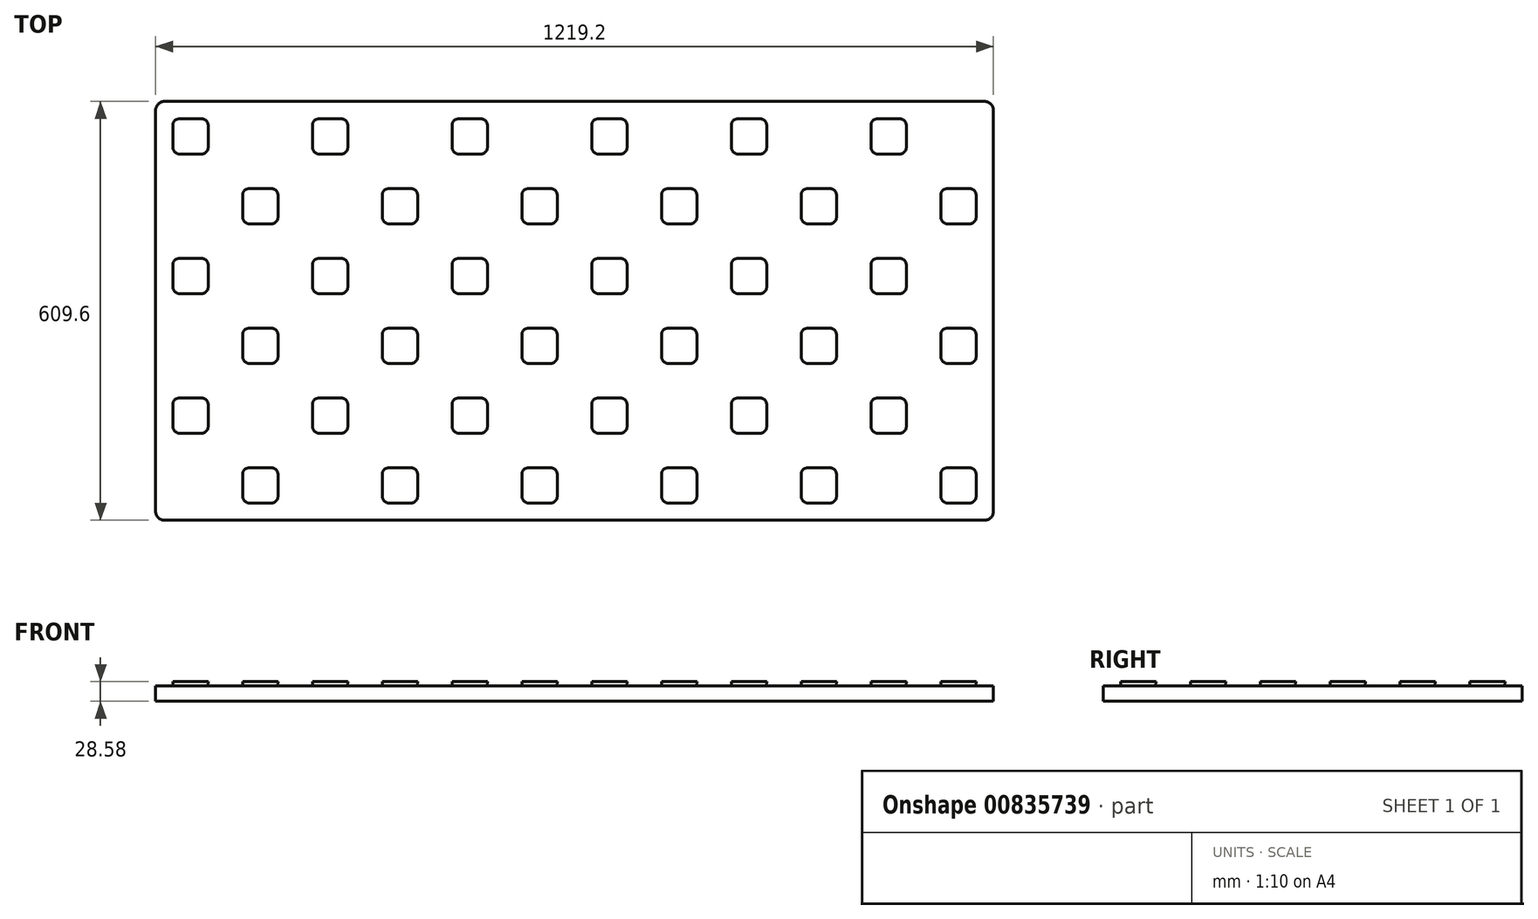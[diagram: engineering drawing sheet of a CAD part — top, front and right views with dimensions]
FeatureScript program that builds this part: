
annotation { "Feature Type Name" : "Feature", "Feature Type Description" : "" }
export const myFeature = defineFeature(function(context is Context, id is Id, definition is map)
    precondition{}
    {
        {
            var Q0;
            Q0=qCreatedBy(makeId("Top.planeOp"),FACE);
            var sketch = newSketch(context, id + "F0", { "sketchPlane" : qUnion([Q0])});
            skLineSegment(sketch, "E0.bottom", {"start": v(12.7, 0) * mm, "end": v(1206.5, 0) * mm});
            skLineSegment(sketch, "E0.top", {"start": v(12.7, 609.6) * mm, "end": v(1206.5, 609.6) * mm});
            skLineSegment(sketch, "E0.left", {"start": v(0, 12.7) * mm, "end": v(0, 596.9) * mm});
            skLineSegment(sketch, "E0.right", {"start": v(1219.2, 12.7) * mm, "end": v(1219.2, 596.9) * mm});
            skPoint(sketch, "E1.visualSharp", {"position": v(0, 609.6) * mm});
            skArc(sketch, "E1.filletArc", {"start": v(12.7, 609.6) * mm, "mid": v(3.72, 605.88) * mm, "end": v(0, 596.9) * mm});
            skPoint(sketch, "E2.visualSharp", {"position": v(1219.2, 609.6) * mm});
            skArc(sketch, "E2.filletArc", {"start": v(1219.2, 596.9) * mm, "mid": v(1215.48, 605.88) * mm, "end": v(1206.5, 609.6) * mm});
            skPoint(sketch, "E3.visualSharp", {"position": v(1219.2, 0) * mm});
            skArc(sketch, "E3.filletArc", {"start": v(1206.5, 0) * mm, "mid": v(1215.48, 3.72) * mm, "end": v(1219.2, 12.7) * mm});
            skPoint(sketch, "E4.visualSharp", {"position": v(0, 0) * mm});
            skArc(sketch, "E4.filletArc", {"start": v(0, 12.7) * mm, "mid": v(3.72, 3.72) * mm, "end": v(12.7, 0) * mm});
            skSolve(sketch);
        }
        {
            var Q0;
            Q0 = qSketchRegion(id + "F0", true);
            extrude(context, id + "F1", {"entities" : qUnion([Q0]), "depth" : 22.22 * mm, "offsetDistance" : 25.4 * mm});
        }
        {
            var Q0;
            Q0=makeQuery(id+"F1.opExtrude","CAP_FACE",FACE,{"disambiguationData":[OSD([sQuery(id+"F0.wireOp",EDGE,"E0.bottom"),sQuery(id+"F0.wireOp",EDGE,"E0.top"),sQuery(id+"F0.wireOp",EDGE,"E0.left"),sQuery(id+"F0.wireOp",EDGE,"E0.right"),sQuery(id+"F0.wireOp",EDGE,"E1.filletArc"),sQuery(id+"F0.wireOp",EDGE,"E2.filletArc"),sQuery(id+"F0.wireOp",EDGE,"E3.filletArc"),sQuery(id+"F0.wireOp",EDGE,"E4.filletArc")])],"isStart":false});
            var sketch = newSketch(context, id + "F2", { "sketchPlane" : qUnion([Q0])});
            skLineSegment(sketch, "E5.bottom", {"start": v(66.67, 584.2) * mm, "end": v(34.93, 584.2) * mm});
            skLineSegment(sketch, "E5.top", {"start": v(66.68, 533.4) * mm, "end": v(34.93, 533.4) * mm});
            skLineSegment(sketch, "E5.left", {"start": v(76.2, 574.68) * mm, "end": v(76.2, 542.93) * mm});
            skLineSegment(sketch, "E5.right", {"start": v(25.4, 574.68) * mm, "end": v(25.4, 542.93) * mm});
            skPoint(sketch, "E5.middle", {"position": v(50.8, 558.8) * mm});
            skPoint(sketch, "E6.visualSharp", {"position": v(25.4, 584.2) * mm});
            skArc(sketch, "E6.filletArc", {"start": v(34.93, 584.2) * mm, "mid": v(28.19, 581.41) * mm, "end": v(25.4, 574.68) * mm});
            skPoint(sketch, "E7.visualSharp", {"position": v(76.2, 533.4) * mm});
            skArc(sketch, "E7.filletArc", {"start": v(66.68, 533.4) * mm, "mid": v(73.41, 536.19) * mm, "end": v(76.2, 542.93) * mm});
            skPoint(sketch, "E8.visualSharp", {"position": v(25.4, 533.4) * mm});
            skArc(sketch, "E8.filletArc", {"start": v(25.4, 542.93) * mm, "mid": v(28.19, 536.19) * mm, "end": v(34.93, 533.4) * mm});
            skPoint(sketch, "E9.visualSharp", {"position": v(76.2, 584.2) * mm});
            skArc(sketch, "E9.filletArc", {"start": v(76.2, 574.68) * mm, "mid": v(73.41, 581.41) * mm, "end": v(66.67, 584.2) * mm});
            skArc(sketch, "E10.0.1.0", {"start": v(76.2, 371.48) * mm, "mid": v(73.41, 378.21) * mm, "end": v(66.67, 381) * mm});
            skLineSegment(sketch, "E10.0.1.1", {"start": v(66.68, 330.2) * mm, "end": v(34.93, 330.2) * mm});
            skLineSegment(sketch, "E10.0.1.2", {"start": v(76.2, 371.48) * mm, "end": v(76.2, 339.73) * mm});
            skLineSegment(sketch, "E10.0.1.3", {"start": v(66.67, 381) * mm, "end": v(34.93, 381) * mm});
            skArc(sketch, "E10.0.1.4", {"start": v(25.4, 339.73) * mm, "mid": v(28.19, 332.99) * mm, "end": v(34.93, 330.2) * mm});
            skArc(sketch, "E10.0.1.5", {"start": v(66.68, 330.2) * mm, "mid": v(73.41, 332.99) * mm, "end": v(76.2, 339.73) * mm});
            skLineSegment(sketch, "E10.0.1.6", {"start": v(25.4, 371.48) * mm, "end": v(25.4, 339.73) * mm});
            skArc(sketch, "E10.0.1.7", {"start": v(34.93, 381) * mm, "mid": v(28.19, 378.21) * mm, "end": v(25.4, 371.48) * mm});
            skArc(sketch, "E10.0.2.0", {"start": v(76.2, 168.28) * mm, "mid": v(73.41, 175.01) * mm, "end": v(66.67, 177.8) * mm});
            skLineSegment(sketch, "E10.0.2.1", {"start": v(66.68, 127) * mm, "end": v(34.93, 127) * mm});
            skLineSegment(sketch, "E10.0.2.2", {"start": v(76.2, 168.28) * mm, "end": v(76.2, 136.53) * mm});
            skLineSegment(sketch, "E10.0.2.3", {"start": v(66.67, 177.8) * mm, "end": v(34.93, 177.8) * mm});
            skArc(sketch, "E10.0.2.4", {"start": v(25.4, 136.53) * mm, "mid": v(28.19, 129.79) * mm, "end": v(34.93, 127) * mm});
            skArc(sketch, "E10.0.2.5", {"start": v(66.68, 127) * mm, "mid": v(73.41, 129.79) * mm, "end": v(76.2, 136.53) * mm});
            skLineSegment(sketch, "E10.0.2.6", {"start": v(25.4, 168.28) * mm, "end": v(25.4, 136.53) * mm});
            skArc(sketch, "E10.0.2.7", {"start": v(34.93, 177.8) * mm, "mid": v(28.19, 175.01) * mm, "end": v(25.4, 168.28) * mm});
            skArc(sketch, "E10.1.0.0", {"start": v(279.4, 574.68) * mm, "mid": v(276.61, 581.41) * mm, "end": v(269.88, 584.2) * mm});
            skLineSegment(sketch, "E10.1.0.1", {"start": v(269.88, 533.4) * mm, "end": v(238.13, 533.4) * mm});
            skLineSegment(sketch, "E10.1.0.2", {"start": v(279.4, 574.68) * mm, "end": v(279.4, 542.93) * mm});
            skLineSegment(sketch, "E10.1.0.3", {"start": v(269.88, 584.2) * mm, "end": v(238.13, 584.2) * mm});
            skArc(sketch, "E10.1.0.4", {"start": v(228.6, 542.93) * mm, "mid": v(231.39, 536.19) * mm, "end": v(238.13, 533.4) * mm});
            skArc(sketch, "E10.1.0.5", {"start": v(269.88, 533.4) * mm, "mid": v(276.61, 536.19) * mm, "end": v(279.4, 542.93) * mm});
            skLineSegment(sketch, "E10.1.0.6", {"start": v(228.6, 574.68) * mm, "end": v(228.6, 542.93) * mm});
            skArc(sketch, "E10.1.0.7", {"start": v(238.13, 584.2) * mm, "mid": v(231.39, 581.41) * mm, "end": v(228.6, 574.68) * mm});
            skArc(sketch, "E10.1.1.0", {"start": v(279.4, 371.48) * mm, "mid": v(276.61, 378.21) * mm, "end": v(269.88, 381) * mm});
            skLineSegment(sketch, "E10.1.1.1", {"start": v(269.88, 330.2) * mm, "end": v(238.13, 330.2) * mm});
            skLineSegment(sketch, "E10.1.1.2", {"start": v(279.4, 371.48) * mm, "end": v(279.4, 339.73) * mm});
            skLineSegment(sketch, "E10.1.1.3", {"start": v(269.88, 381) * mm, "end": v(238.13, 381) * mm});
            skArc(sketch, "E10.1.1.4", {"start": v(228.6, 339.73) * mm, "mid": v(231.39, 332.99) * mm, "end": v(238.13, 330.2) * mm});
            skArc(sketch, "E10.1.1.5", {"start": v(269.88, 330.2) * mm, "mid": v(276.61, 332.99) * mm, "end": v(279.4, 339.73) * mm});
            skLineSegment(sketch, "E10.1.1.6", {"start": v(228.6, 371.48) * mm, "end": v(228.6, 339.73) * mm});
            skArc(sketch, "E10.1.1.7", {"start": v(238.13, 381) * mm, "mid": v(231.39, 378.21) * mm, "end": v(228.6, 371.48) * mm});
            skArc(sketch, "E10.1.2.0", {"start": v(279.4, 168.28) * mm, "mid": v(276.61, 175.01) * mm, "end": v(269.88, 177.8) * mm});
            skLineSegment(sketch, "E10.1.2.1", {"start": v(269.88, 127) * mm, "end": v(238.13, 127) * mm});
            skLineSegment(sketch, "E10.1.2.2", {"start": v(279.4, 168.28) * mm, "end": v(279.4, 136.53) * mm});
            skLineSegment(sketch, "E10.1.2.3", {"start": v(269.88, 177.8) * mm, "end": v(238.13, 177.8) * mm});
            skArc(sketch, "E10.1.2.4", {"start": v(228.6, 136.53) * mm, "mid": v(231.39, 129.79) * mm, "end": v(238.13, 127) * mm});
            skArc(sketch, "E10.1.2.5", {"start": v(269.88, 127) * mm, "mid": v(276.61, 129.79) * mm, "end": v(279.4, 136.53) * mm});
            skLineSegment(sketch, "E10.1.2.6", {"start": v(228.6, 168.28) * mm, "end": v(228.6, 136.53) * mm});
            skArc(sketch, "E10.1.2.7", {"start": v(238.13, 177.8) * mm, "mid": v(231.39, 175.01) * mm, "end": v(228.6, 168.28) * mm});
            skArc(sketch, "E10.2.0.0", {"start": v(482.6, 574.68) * mm, "mid": v(479.81, 581.41) * mm, "end": v(473.08, 584.2) * mm});
            skLineSegment(sketch, "E10.2.0.1", {"start": v(473.08, 533.4) * mm, "end": v(441.33, 533.4) * mm});
            skLineSegment(sketch, "E10.2.0.2", {"start": v(482.6, 574.68) * mm, "end": v(482.6, 542.93) * mm});
            skLineSegment(sketch, "E10.2.0.3", {"start": v(473.08, 584.2) * mm, "end": v(441.33, 584.2) * mm});
            skArc(sketch, "E10.2.0.4", {"start": v(431.8, 542.93) * mm, "mid": v(434.59, 536.19) * mm, "end": v(441.33, 533.4) * mm});
            skArc(sketch, "E10.2.0.5", {"start": v(473.08, 533.4) * mm, "mid": v(479.81, 536.19) * mm, "end": v(482.6, 542.93) * mm});
            skLineSegment(sketch, "E10.2.0.6", {"start": v(431.8, 574.68) * mm, "end": v(431.8, 542.93) * mm});
            skArc(sketch, "E10.2.0.7", {"start": v(441.33, 584.2) * mm, "mid": v(434.59, 581.41) * mm, "end": v(431.8, 574.68) * mm});
            skArc(sketch, "E10.2.1.0", {"start": v(482.6, 371.48) * mm, "mid": v(479.81, 378.21) * mm, "end": v(473.08, 381) * mm});
            skLineSegment(sketch, "E10.2.1.1", {"start": v(473.08, 330.2) * mm, "end": v(441.33, 330.2) * mm});
            skLineSegment(sketch, "E10.2.1.2", {"start": v(482.6, 371.48) * mm, "end": v(482.6, 339.73) * mm});
            skLineSegment(sketch, "E10.2.1.3", {"start": v(473.08, 381) * mm, "end": v(441.33, 381) * mm});
            skArc(sketch, "E10.2.1.4", {"start": v(431.8, 339.73) * mm, "mid": v(434.59, 332.99) * mm, "end": v(441.33, 330.2) * mm});
            skArc(sketch, "E10.2.1.5", {"start": v(473.08, 330.2) * mm, "mid": v(479.81, 332.99) * mm, "end": v(482.6, 339.73) * mm});
            skLineSegment(sketch, "E10.2.1.6", {"start": v(431.8, 371.48) * mm, "end": v(431.8, 339.73) * mm});
            skArc(sketch, "E10.2.1.7", {"start": v(441.33, 381) * mm, "mid": v(434.59, 378.21) * mm, "end": v(431.8, 371.48) * mm});
            skArc(sketch, "E10.2.2.0", {"start": v(482.6, 168.28) * mm, "mid": v(479.81, 175.01) * mm, "end": v(473.08, 177.8) * mm});
            skLineSegment(sketch, "E10.2.2.1", {"start": v(473.08, 127) * mm, "end": v(441.33, 127) * mm});
            skLineSegment(sketch, "E10.2.2.2", {"start": v(482.6, 168.28) * mm, "end": v(482.6, 136.53) * mm});
            skLineSegment(sketch, "E10.2.2.3", {"start": v(473.08, 177.8) * mm, "end": v(441.33, 177.8) * mm});
            skArc(sketch, "E10.2.2.4", {"start": v(431.8, 136.53) * mm, "mid": v(434.59, 129.79) * mm, "end": v(441.33, 127) * mm});
            skArc(sketch, "E10.2.2.5", {"start": v(473.08, 127) * mm, "mid": v(479.81, 129.79) * mm, "end": v(482.6, 136.53) * mm});
            skLineSegment(sketch, "E10.2.2.6", {"start": v(431.8, 168.28) * mm, "end": v(431.8, 136.53) * mm});
            skArc(sketch, "E10.2.2.7", {"start": v(441.33, 177.8) * mm, "mid": v(434.59, 175.01) * mm, "end": v(431.8, 168.28) * mm});
            skArc(sketch, "E10.3.0.0", {"start": v(685.8, 574.68) * mm, "mid": v(683.01, 581.41) * mm, "end": v(676.27, 584.2) * mm});
            skLineSegment(sketch, "E10.3.0.1", {"start": v(676.28, 533.4) * mm, "end": v(644.52, 533.4) * mm});
            skLineSegment(sketch, "E10.3.0.2", {"start": v(685.8, 574.68) * mm, "end": v(685.8, 542.93) * mm});
            skLineSegment(sketch, "E10.3.0.3", {"start": v(676.28, 584.2) * mm, "end": v(644.52, 584.2) * mm});
            skArc(sketch, "E10.3.0.4", {"start": v(635, 542.93) * mm, "mid": v(637.79, 536.19) * mm, "end": v(644.52, 533.4) * mm});
            skArc(sketch, "E10.3.0.5", {"start": v(676.28, 533.4) * mm, "mid": v(683.01, 536.19) * mm, "end": v(685.8, 542.93) * mm});
            skLineSegment(sketch, "E10.3.0.6", {"start": v(635, 574.68) * mm, "end": v(635, 542.93) * mm});
            skArc(sketch, "E10.3.0.7", {"start": v(644.52, 584.2) * mm, "mid": v(637.79, 581.41) * mm, "end": v(635, 574.68) * mm});
            skArc(sketch, "E10.3.1.0", {"start": v(685.8, 371.48) * mm, "mid": v(683.01, 378.21) * mm, "end": v(676.27, 381) * mm});
            skLineSegment(sketch, "E10.3.1.1", {"start": v(676.28, 330.2) * mm, "end": v(644.52, 330.2) * mm});
            skLineSegment(sketch, "E10.3.1.2", {"start": v(685.8, 371.48) * mm, "end": v(685.8, 339.73) * mm});
            skLineSegment(sketch, "E10.3.1.3", {"start": v(676.28, 381) * mm, "end": v(644.52, 381) * mm});
            skArc(sketch, "E10.3.1.4", {"start": v(635, 339.73) * mm, "mid": v(637.79, 332.99) * mm, "end": v(644.52, 330.2) * mm});
            skArc(sketch, "E10.3.1.5", {"start": v(676.28, 330.2) * mm, "mid": v(683.01, 332.99) * mm, "end": v(685.8, 339.73) * mm});
            skLineSegment(sketch, "E10.3.1.6", {"start": v(635, 371.48) * mm, "end": v(635, 339.73) * mm});
            skArc(sketch, "E10.3.1.7", {"start": v(644.52, 381) * mm, "mid": v(637.79, 378.21) * mm, "end": v(635, 371.48) * mm});
            skArc(sketch, "E10.3.2.0", {"start": v(685.8, 168.28) * mm, "mid": v(683.01, 175.01) * mm, "end": v(676.27, 177.8) * mm});
            skLineSegment(sketch, "E10.3.2.1", {"start": v(676.28, 127) * mm, "end": v(644.52, 127) * mm});
            skLineSegment(sketch, "E10.3.2.2", {"start": v(685.8, 168.28) * mm, "end": v(685.8, 136.53) * mm});
            skLineSegment(sketch, "E10.3.2.3", {"start": v(676.28, 177.8) * mm, "end": v(644.52, 177.8) * mm});
            skArc(sketch, "E10.3.2.4", {"start": v(635, 136.53) * mm, "mid": v(637.79, 129.79) * mm, "end": v(644.52, 127) * mm});
            skArc(sketch, "E10.3.2.5", {"start": v(676.28, 127) * mm, "mid": v(683.01, 129.79) * mm, "end": v(685.8, 136.53) * mm});
            skLineSegment(sketch, "E10.3.2.6", {"start": v(635, 168.28) * mm, "end": v(635, 136.53) * mm});
            skArc(sketch, "E10.3.2.7", {"start": v(644.52, 177.8) * mm, "mid": v(637.79, 175.01) * mm, "end": v(635, 168.28) * mm});
            skArc(sketch, "E10.4.0.0", {"start": v(889, 574.68) * mm, "mid": v(886.21, 581.41) * mm, "end": v(879.48, 584.2) * mm});
            skLineSegment(sketch, "E10.4.0.1", {"start": v(879.48, 533.4) * mm, "end": v(847.73, 533.4) * mm});
            skLineSegment(sketch, "E10.4.0.2", {"start": v(889, 574.68) * mm, "end": v(889, 542.93) * mm});
            skLineSegment(sketch, "E10.4.0.3", {"start": v(879.48, 584.2) * mm, "end": v(847.73, 584.2) * mm});
            skArc(sketch, "E10.4.0.4", {"start": v(838.2, 542.93) * mm, "mid": v(840.99, 536.19) * mm, "end": v(847.73, 533.4) * mm});
            skArc(sketch, "E10.4.0.5", {"start": v(879.48, 533.4) * mm, "mid": v(886.21, 536.19) * mm, "end": v(889, 542.93) * mm});
            skLineSegment(sketch, "E10.4.0.6", {"start": v(838.2, 574.68) * mm, "end": v(838.2, 542.93) * mm});
            skArc(sketch, "E10.4.0.7", {"start": v(847.73, 584.2) * mm, "mid": v(840.99, 581.41) * mm, "end": v(838.2, 574.68) * mm});
            skArc(sketch, "E10.4.1.0", {"start": v(889, 371.48) * mm, "mid": v(886.21, 378.21) * mm, "end": v(879.48, 381) * mm});
            skLineSegment(sketch, "E10.4.1.1", {"start": v(879.48, 330.2) * mm, "end": v(847.73, 330.2) * mm});
            skLineSegment(sketch, "E10.4.1.2", {"start": v(889, 371.48) * mm, "end": v(889, 339.73) * mm});
            skLineSegment(sketch, "E10.4.1.3", {"start": v(879.48, 381) * mm, "end": v(847.73, 381) * mm});
            skArc(sketch, "E10.4.1.4", {"start": v(838.2, 339.73) * mm, "mid": v(840.99, 332.99) * mm, "end": v(847.73, 330.2) * mm});
            skArc(sketch, "E10.4.1.5", {"start": v(879.48, 330.2) * mm, "mid": v(886.21, 332.99) * mm, "end": v(889, 339.73) * mm});
            skLineSegment(sketch, "E10.4.1.6", {"start": v(838.2, 371.48) * mm, "end": v(838.2, 339.73) * mm});
            skArc(sketch, "E10.4.1.7", {"start": v(847.73, 381) * mm, "mid": v(840.99, 378.21) * mm, "end": v(838.2, 371.48) * mm});
            skArc(sketch, "E10.4.2.0", {"start": v(889, 168.28) * mm, "mid": v(886.21, 175.01) * mm, "end": v(879.48, 177.8) * mm});
            skLineSegment(sketch, "E10.4.2.1", {"start": v(879.48, 127) * mm, "end": v(847.73, 127) * mm});
            skLineSegment(sketch, "E10.4.2.2", {"start": v(889, 168.28) * mm, "end": v(889, 136.53) * mm});
            skLineSegment(sketch, "E10.4.2.3", {"start": v(879.48, 177.8) * mm, "end": v(847.73, 177.8) * mm});
            skArc(sketch, "E10.4.2.4", {"start": v(838.2, 136.53) * mm, "mid": v(840.99, 129.79) * mm, "end": v(847.73, 127) * mm});
            skArc(sketch, "E10.4.2.5", {"start": v(879.48, 127) * mm, "mid": v(886.21, 129.79) * mm, "end": v(889, 136.53) * mm});
            skLineSegment(sketch, "E10.4.2.6", {"start": v(838.2, 168.28) * mm, "end": v(838.2, 136.53) * mm});
            skArc(sketch, "E10.4.2.7", {"start": v(847.73, 177.8) * mm, "mid": v(840.99, 175.01) * mm, "end": v(838.2, 168.28) * mm});
            skArc(sketch, "E10.5.0.0", {"start": v(1092.2, 574.68) * mm, "mid": v(1089.41, 581.41) * mm, "end": v(1082.67, 584.2) * mm});
            skLineSegment(sketch, "E10.5.0.1", {"start": v(1082.67, 533.4) * mm, "end": v(1050.93, 533.4) * mm});
            skLineSegment(sketch, "E10.5.0.2", {"start": v(1092.2, 574.68) * mm, "end": v(1092.2, 542.93) * mm});
            skLineSegment(sketch, "E10.5.0.3", {"start": v(1082.67, 584.2) * mm, "end": v(1050.93, 584.2) * mm});
            skArc(sketch, "E10.5.0.4", {"start": v(1041.4, 542.93) * mm, "mid": v(1044.19, 536.19) * mm, "end": v(1050.93, 533.4) * mm});
            skArc(sketch, "E10.5.0.5", {"start": v(1082.67, 533.4) * mm, "mid": v(1089.41, 536.19) * mm, "end": v(1092.2, 542.93) * mm});
            skLineSegment(sketch, "E10.5.0.6", {"start": v(1041.4, 574.68) * mm, "end": v(1041.4, 542.93) * mm});
            skArc(sketch, "E10.5.0.7", {"start": v(1050.93, 584.2) * mm, "mid": v(1044.19, 581.41) * mm, "end": v(1041.4, 574.68) * mm});
            skArc(sketch, "E10.5.1.0", {"start": v(1092.2, 371.48) * mm, "mid": v(1089.41, 378.21) * mm, "end": v(1082.67, 381) * mm});
            skLineSegment(sketch, "E10.5.1.1", {"start": v(1082.67, 330.2) * mm, "end": v(1050.93, 330.2) * mm});
            skLineSegment(sketch, "E10.5.1.2", {"start": v(1092.2, 371.48) * mm, "end": v(1092.2, 339.73) * mm});
            skLineSegment(sketch, "E10.5.1.3", {"start": v(1082.67, 381) * mm, "end": v(1050.93, 381) * mm});
            skArc(sketch, "E10.5.1.4", {"start": v(1041.4, 339.73) * mm, "mid": v(1044.19, 332.99) * mm, "end": v(1050.93, 330.2) * mm});
            skArc(sketch, "E10.5.1.5", {"start": v(1082.67, 330.2) * mm, "mid": v(1089.41, 332.99) * mm, "end": v(1092.2, 339.73) * mm});
            skLineSegment(sketch, "E10.5.1.6", {"start": v(1041.4, 371.48) * mm, "end": v(1041.4, 339.73) * mm});
            skArc(sketch, "E10.5.1.7", {"start": v(1050.93, 381) * mm, "mid": v(1044.19, 378.21) * mm, "end": v(1041.4, 371.48) * mm});
            skArc(sketch, "E10.5.2.0", {"start": v(1092.2, 168.28) * mm, "mid": v(1089.41, 175.01) * mm, "end": v(1082.67, 177.8) * mm});
            skLineSegment(sketch, "E10.5.2.1", {"start": v(1082.67, 127) * mm, "end": v(1050.93, 127) * mm});
            skLineSegment(sketch, "E10.5.2.2", {"start": v(1092.2, 168.28) * mm, "end": v(1092.2, 136.53) * mm});
            skLineSegment(sketch, "E10.5.2.3", {"start": v(1082.67, 177.8) * mm, "end": v(1050.93, 177.8) * mm});
            skArc(sketch, "E10.5.2.4", {"start": v(1041.4, 136.53) * mm, "mid": v(1044.19, 129.79) * mm, "end": v(1050.93, 127) * mm});
            skArc(sketch, "E10.5.2.5", {"start": v(1082.67, 127) * mm, "mid": v(1089.41, 129.79) * mm, "end": v(1092.2, 136.53) * mm});
            skLineSegment(sketch, "E10.5.2.6", {"start": v(1041.4, 168.28) * mm, "end": v(1041.4, 136.53) * mm});
            skArc(sketch, "E10.5.2.7", {"start": v(1050.93, 177.8) * mm, "mid": v(1044.19, 175.01) * mm, "end": v(1041.4, 168.28) * mm});
            skLineSegment(sketch, "E10.direction1", {"start": v(25.4, 542.93) * mm, "end": v(228.6, 542.93) * mm, "construction": true});
            skLineSegment(sketch, "E10.direction2", {"start": v(25.4, 542.93) * mm, "end": v(25.4, 339.73) * mm, "construction": true});
            skLineSegment(sketch, "E11.bottom", {"start": v(168.27, 482.6) * mm, "end": v(136.52, 482.6) * mm});
            skLineSegment(sketch, "E11.top", {"start": v(168.27, 431.8) * mm, "end": v(136.52, 431.8) * mm});
            skLineSegment(sketch, "E11.left", {"start": v(177.8, 473.08) * mm, "end": v(177.8, 441.33) * mm});
            skLineSegment(sketch, "E11.right", {"start": v(127, 473.08) * mm, "end": v(127, 441.33) * mm});
            skPoint(sketch, "E11.middle", {"position": v(152.4, 457.2) * mm});
            skPoint(sketch, "E12.visualSharp", {"position": v(127, 482.6) * mm});
            skArc(sketch, "E12.filletArc", {"start": v(136.52, 482.6) * mm, "mid": v(129.79, 479.81) * mm, "end": v(127, 473.08) * mm});
            skPoint(sketch, "E13.visualSharp", {"position": v(177.8, 482.6) * mm});
            skArc(sketch, "E13.filletArc", {"start": v(177.8, 473.08) * mm, "mid": v(175.01, 479.81) * mm, "end": v(168.27, 482.6) * mm});
            skPoint(sketch, "E14.visualSharp", {"position": v(177.8, 431.8) * mm});
            skArc(sketch, "E14.filletArc", {"start": v(168.27, 431.8) * mm, "mid": v(175.01, 434.59) * mm, "end": v(177.8, 441.33) * mm});
            skPoint(sketch, "E15.visualSharp", {"position": v(127, 431.8) * mm});
            skArc(sketch, "E15.filletArc", {"start": v(127, 441.33) * mm, "mid": v(129.79, 434.59) * mm, "end": v(136.52, 431.8) * mm});
            skArc(sketch, "E16.0.1.0", {"start": v(168.27, 228.6) * mm, "mid": v(175.01, 231.39) * mm, "end": v(177.8, 238.13) * mm});
            skLineSegment(sketch, "E16.0.1.1", {"start": v(168.27, 228.6) * mm, "end": v(136.52, 228.6) * mm});
            skLineSegment(sketch, "E16.0.1.2", {"start": v(127, 269.88) * mm, "end": v(127, 238.13) * mm});
            skArc(sketch, "E16.0.1.3", {"start": v(136.52, 279.4) * mm, "mid": v(129.79, 276.61) * mm, "end": v(127, 269.88) * mm});
            skLineSegment(sketch, "E16.0.1.4", {"start": v(177.8, 269.88) * mm, "end": v(177.8, 238.13) * mm});
            skLineSegment(sketch, "E16.0.1.5", {"start": v(168.27, 279.4) * mm, "end": v(136.52, 279.4) * mm});
            skArc(sketch, "E16.0.1.6", {"start": v(177.8, 269.88) * mm, "mid": v(175.01, 276.61) * mm, "end": v(168.27, 279.4) * mm});
            skArc(sketch, "E16.0.1.7", {"start": v(127, 238.13) * mm, "mid": v(129.79, 231.39) * mm, "end": v(136.52, 228.6) * mm});
            skArc(sketch, "E16.0.2.0", {"start": v(168.27, 25.4) * mm, "mid": v(175.01, 28.19) * mm, "end": v(177.8, 34.93) * mm});
            skLineSegment(sketch, "E16.0.2.1", {"start": v(168.27, 25.4) * mm, "end": v(136.52, 25.4) * mm});
            skLineSegment(sketch, "E16.0.2.2", {"start": v(127, 66.68) * mm, "end": v(127, 34.93) * mm});
            skArc(sketch, "E16.0.2.3", {"start": v(136.52, 76.2) * mm, "mid": v(129.79, 73.41) * mm, "end": v(127, 66.68) * mm});
            skLineSegment(sketch, "E16.0.2.4", {"start": v(177.8, 66.68) * mm, "end": v(177.8, 34.93) * mm});
            skLineSegment(sketch, "E16.0.2.5", {"start": v(168.27, 76.2) * mm, "end": v(136.52, 76.2) * mm});
            skArc(sketch, "E16.0.2.6", {"start": v(177.8, 66.68) * mm, "mid": v(175.01, 73.41) * mm, "end": v(168.27, 76.2) * mm});
            skArc(sketch, "E16.0.2.7", {"start": v(127, 34.93) * mm, "mid": v(129.79, 28.19) * mm, "end": v(136.52, 25.4) * mm});
            skArc(sketch, "E16.1.0.0", {"start": v(371.47, 431.8) * mm, "mid": v(378.21, 434.59) * mm, "end": v(381, 441.33) * mm});
            skLineSegment(sketch, "E16.1.0.1", {"start": v(371.47, 431.8) * mm, "end": v(339.72, 431.8) * mm});
            skLineSegment(sketch, "E16.1.0.2", {"start": v(330.2, 473.08) * mm, "end": v(330.2, 441.33) * mm});
            skArc(sketch, "E16.1.0.3", {"start": v(339.72, 482.6) * mm, "mid": v(332.99, 479.81) * mm, "end": v(330.2, 473.08) * mm});
            skLineSegment(sketch, "E16.1.0.4", {"start": v(381, 473.08) * mm, "end": v(381, 441.33) * mm});
            skLineSegment(sketch, "E16.1.0.5", {"start": v(371.47, 482.6) * mm, "end": v(339.72, 482.6) * mm});
            skArc(sketch, "E16.1.0.6", {"start": v(381, 473.08) * mm, "mid": v(378.21, 479.81) * mm, "end": v(371.47, 482.6) * mm});
            skArc(sketch, "E16.1.0.7", {"start": v(330.2, 441.33) * mm, "mid": v(332.99, 434.59) * mm, "end": v(339.72, 431.8) * mm});
            skArc(sketch, "E16.1.1.0", {"start": v(371.47, 228.6) * mm, "mid": v(378.21, 231.39) * mm, "end": v(381, 238.13) * mm});
            skLineSegment(sketch, "E16.1.1.1", {"start": v(371.47, 228.6) * mm, "end": v(339.72, 228.6) * mm});
            skLineSegment(sketch, "E16.1.1.2", {"start": v(330.2, 269.88) * mm, "end": v(330.2, 238.13) * mm});
            skArc(sketch, "E16.1.1.3", {"start": v(339.72, 279.4) * mm, "mid": v(332.99, 276.61) * mm, "end": v(330.2, 269.88) * mm});
            skLineSegment(sketch, "E16.1.1.4", {"start": v(381, 269.88) * mm, "end": v(381, 238.13) * mm});
            skLineSegment(sketch, "E16.1.1.5", {"start": v(371.47, 279.4) * mm, "end": v(339.72, 279.4) * mm});
            skArc(sketch, "E16.1.1.6", {"start": v(381, 269.88) * mm, "mid": v(378.21, 276.61) * mm, "end": v(371.47, 279.4) * mm});
            skArc(sketch, "E16.1.1.7", {"start": v(330.2, 238.13) * mm, "mid": v(332.99, 231.39) * mm, "end": v(339.72, 228.6) * mm});
            skArc(sketch, "E16.1.2.0", {"start": v(371.47, 25.4) * mm, "mid": v(378.21, 28.19) * mm, "end": v(381, 34.93) * mm});
            skLineSegment(sketch, "E16.1.2.1", {"start": v(371.47, 25.4) * mm, "end": v(339.72, 25.4) * mm});
            skLineSegment(sketch, "E16.1.2.2", {"start": v(330.2, 66.68) * mm, "end": v(330.2, 34.93) * mm});
            skArc(sketch, "E16.1.2.3", {"start": v(339.72, 76.2) * mm, "mid": v(332.99, 73.41) * mm, "end": v(330.2, 66.68) * mm});
            skLineSegment(sketch, "E16.1.2.4", {"start": v(381, 66.68) * mm, "end": v(381, 34.93) * mm});
            skLineSegment(sketch, "E16.1.2.5", {"start": v(371.47, 76.2) * mm, "end": v(339.72, 76.2) * mm});
            skArc(sketch, "E16.1.2.6", {"start": v(381, 66.68) * mm, "mid": v(378.21, 73.41) * mm, "end": v(371.47, 76.2) * mm});
            skArc(sketch, "E16.1.2.7", {"start": v(330.2, 34.93) * mm, "mid": v(332.99, 28.19) * mm, "end": v(339.72, 25.4) * mm});
            skArc(sketch, "E16.2.0.0", {"start": v(574.67, 431.8) * mm, "mid": v(581.41, 434.59) * mm, "end": v(584.2, 441.33) * mm});
            skLineSegment(sketch, "E16.2.0.1", {"start": v(574.67, 431.8) * mm, "end": v(542.92, 431.8) * mm});
            skLineSegment(sketch, "E16.2.0.2", {"start": v(533.4, 473.08) * mm, "end": v(533.4, 441.33) * mm});
            skArc(sketch, "E16.2.0.3", {"start": v(542.92, 482.6) * mm, "mid": v(536.19, 479.81) * mm, "end": v(533.4, 473.08) * mm});
            skLineSegment(sketch, "E16.2.0.4", {"start": v(584.2, 473.08) * mm, "end": v(584.2, 441.33) * mm});
            skLineSegment(sketch, "E16.2.0.5", {"start": v(574.67, 482.6) * mm, "end": v(542.92, 482.6) * mm});
            skArc(sketch, "E16.2.0.6", {"start": v(584.2, 473.08) * mm, "mid": v(581.41, 479.81) * mm, "end": v(574.67, 482.6) * mm});
            skArc(sketch, "E16.2.0.7", {"start": v(533.4, 441.33) * mm, "mid": v(536.19, 434.59) * mm, "end": v(542.92, 431.8) * mm});
            skArc(sketch, "E16.2.1.0", {"start": v(574.67, 228.6) * mm, "mid": v(581.41, 231.39) * mm, "end": v(584.2, 238.13) * mm});
            skLineSegment(sketch, "E16.2.1.1", {"start": v(574.67, 228.6) * mm, "end": v(542.92, 228.6) * mm});
            skLineSegment(sketch, "E16.2.1.2", {"start": v(533.4, 269.88) * mm, "end": v(533.4, 238.13) * mm});
            skArc(sketch, "E16.2.1.3", {"start": v(542.92, 279.4) * mm, "mid": v(536.19, 276.61) * mm, "end": v(533.4, 269.88) * mm});
            skLineSegment(sketch, "E16.2.1.4", {"start": v(584.2, 269.88) * mm, "end": v(584.2, 238.13) * mm});
            skLineSegment(sketch, "E16.2.1.5", {"start": v(574.67, 279.4) * mm, "end": v(542.92, 279.4) * mm});
            skArc(sketch, "E16.2.1.6", {"start": v(584.2, 269.88) * mm, "mid": v(581.41, 276.61) * mm, "end": v(574.67, 279.4) * mm});
            skArc(sketch, "E16.2.1.7", {"start": v(533.4, 238.13) * mm, "mid": v(536.19, 231.39) * mm, "end": v(542.92, 228.6) * mm});
            skArc(sketch, "E16.2.2.0", {"start": v(574.67, 25.4) * mm, "mid": v(581.41, 28.19) * mm, "end": v(584.2, 34.93) * mm});
            skLineSegment(sketch, "E16.2.2.1", {"start": v(574.67, 25.4) * mm, "end": v(542.92, 25.4) * mm});
            skLineSegment(sketch, "E16.2.2.2", {"start": v(533.4, 66.68) * mm, "end": v(533.4, 34.93) * mm});
            skArc(sketch, "E16.2.2.3", {"start": v(542.92, 76.2) * mm, "mid": v(536.19, 73.41) * mm, "end": v(533.4, 66.68) * mm});
            skLineSegment(sketch, "E16.2.2.4", {"start": v(584.2, 66.68) * mm, "end": v(584.2, 34.93) * mm});
            skLineSegment(sketch, "E16.2.2.5", {"start": v(574.67, 76.2) * mm, "end": v(542.92, 76.2) * mm});
            skArc(sketch, "E16.2.2.6", {"start": v(584.2, 66.68) * mm, "mid": v(581.41, 73.41) * mm, "end": v(574.67, 76.2) * mm});
            skArc(sketch, "E16.2.2.7", {"start": v(533.4, 34.93) * mm, "mid": v(536.19, 28.19) * mm, "end": v(542.92, 25.4) * mm});
            skArc(sketch, "E16.3.0.0", {"start": v(777.87, 431.8) * mm, "mid": v(784.61, 434.59) * mm, "end": v(787.4, 441.33) * mm});
            skLineSegment(sketch, "E16.3.0.1", {"start": v(777.87, 431.8) * mm, "end": v(746.12, 431.8) * mm});
            skLineSegment(sketch, "E16.3.0.2", {"start": v(736.6, 473.08) * mm, "end": v(736.6, 441.33) * mm});
            skArc(sketch, "E16.3.0.3", {"start": v(746.12, 482.6) * mm, "mid": v(739.39, 479.81) * mm, "end": v(736.6, 473.08) * mm});
            skLineSegment(sketch, "E16.3.0.4", {"start": v(787.4, 473.08) * mm, "end": v(787.4, 441.33) * mm});
            skLineSegment(sketch, "E16.3.0.5", {"start": v(777.87, 482.6) * mm, "end": v(746.12, 482.6) * mm});
            skArc(sketch, "E16.3.0.6", {"start": v(787.4, 473.08) * mm, "mid": v(784.61, 479.81) * mm, "end": v(777.87, 482.6) * mm});
            skArc(sketch, "E16.3.0.7", {"start": v(736.6, 441.33) * mm, "mid": v(739.39, 434.59) * mm, "end": v(746.12, 431.8) * mm});
            skArc(sketch, "E16.3.1.0", {"start": v(777.87, 228.6) * mm, "mid": v(784.61, 231.39) * mm, "end": v(787.4, 238.13) * mm});
            skLineSegment(sketch, "E16.3.1.1", {"start": v(777.87, 228.6) * mm, "end": v(746.12, 228.6) * mm});
            skLineSegment(sketch, "E16.3.1.2", {"start": v(736.6, 269.88) * mm, "end": v(736.6, 238.13) * mm});
            skArc(sketch, "E16.3.1.3", {"start": v(746.12, 279.4) * mm, "mid": v(739.39, 276.61) * mm, "end": v(736.6, 269.88) * mm});
            skLineSegment(sketch, "E16.3.1.4", {"start": v(787.4, 269.88) * mm, "end": v(787.4, 238.13) * mm});
            skLineSegment(sketch, "E16.3.1.5", {"start": v(777.87, 279.4) * mm, "end": v(746.12, 279.4) * mm});
            skArc(sketch, "E16.3.1.6", {"start": v(787.4, 269.88) * mm, "mid": v(784.61, 276.61) * mm, "end": v(777.87, 279.4) * mm});
            skArc(sketch, "E16.3.1.7", {"start": v(736.6, 238.13) * mm, "mid": v(739.39, 231.39) * mm, "end": v(746.12, 228.6) * mm});
            skArc(sketch, "E16.3.2.0", {"start": v(777.87, 25.4) * mm, "mid": v(784.61, 28.19) * mm, "end": v(787.4, 34.93) * mm});
            skLineSegment(sketch, "E16.3.2.1", {"start": v(777.87, 25.4) * mm, "end": v(746.12, 25.4) * mm});
            skLineSegment(sketch, "E16.3.2.2", {"start": v(736.6, 66.68) * mm, "end": v(736.6, 34.93) * mm});
            skArc(sketch, "E16.3.2.3", {"start": v(746.12, 76.2) * mm, "mid": v(739.39, 73.41) * mm, "end": v(736.6, 66.68) * mm});
            skLineSegment(sketch, "E16.3.2.4", {"start": v(787.4, 66.68) * mm, "end": v(787.4, 34.93) * mm});
            skLineSegment(sketch, "E16.3.2.5", {"start": v(777.87, 76.2) * mm, "end": v(746.12, 76.2) * mm});
            skArc(sketch, "E16.3.2.6", {"start": v(787.4, 66.68) * mm, "mid": v(784.61, 73.41) * mm, "end": v(777.87, 76.2) * mm});
            skArc(sketch, "E16.3.2.7", {"start": v(736.6, 34.93) * mm, "mid": v(739.39, 28.19) * mm, "end": v(746.12, 25.4) * mm});
            skArc(sketch, "E16.4.0.0", {"start": v(981.07, 431.8) * mm, "mid": v(987.81, 434.59) * mm, "end": v(990.6, 441.33) * mm});
            skLineSegment(sketch, "E16.4.0.1", {"start": v(981.07, 431.8) * mm, "end": v(949.32, 431.8) * mm});
            skLineSegment(sketch, "E16.4.0.2", {"start": v(939.8, 473.08) * mm, "end": v(939.8, 441.33) * mm});
            skArc(sketch, "E16.4.0.3", {"start": v(949.32, 482.6) * mm, "mid": v(942.59, 479.81) * mm, "end": v(939.8, 473.08) * mm});
            skLineSegment(sketch, "E16.4.0.4", {"start": v(990.6, 473.08) * mm, "end": v(990.6, 441.33) * mm});
            skLineSegment(sketch, "E16.4.0.5", {"start": v(981.07, 482.6) * mm, "end": v(949.32, 482.6) * mm});
            skArc(sketch, "E16.4.0.6", {"start": v(990.6, 473.08) * mm, "mid": v(987.81, 479.81) * mm, "end": v(981.07, 482.6) * mm});
            skArc(sketch, "E16.4.0.7", {"start": v(939.8, 441.33) * mm, "mid": v(942.59, 434.59) * mm, "end": v(949.32, 431.8) * mm});
            skArc(sketch, "E16.4.1.0", {"start": v(981.07, 228.6) * mm, "mid": v(987.81, 231.39) * mm, "end": v(990.6, 238.13) * mm});
            skLineSegment(sketch, "E16.4.1.1", {"start": v(981.07, 228.6) * mm, "end": v(949.32, 228.6) * mm});
            skLineSegment(sketch, "E16.4.1.2", {"start": v(939.8, 269.88) * mm, "end": v(939.8, 238.13) * mm});
            skArc(sketch, "E16.4.1.3", {"start": v(949.32, 279.4) * mm, "mid": v(942.59, 276.61) * mm, "end": v(939.8, 269.88) * mm});
            skLineSegment(sketch, "E16.4.1.4", {"start": v(990.6, 269.88) * mm, "end": v(990.6, 238.13) * mm});
            skLineSegment(sketch, "E16.4.1.5", {"start": v(981.07, 279.4) * mm, "end": v(949.32, 279.4) * mm});
            skArc(sketch, "E16.4.1.6", {"start": v(990.6, 269.88) * mm, "mid": v(987.81, 276.61) * mm, "end": v(981.07, 279.4) * mm});
            skArc(sketch, "E16.4.1.7", {"start": v(939.8, 238.13) * mm, "mid": v(942.59, 231.39) * mm, "end": v(949.32, 228.6) * mm});
            skArc(sketch, "E16.4.2.0", {"start": v(981.07, 25.4) * mm, "mid": v(987.81, 28.19) * mm, "end": v(990.6, 34.93) * mm});
            skLineSegment(sketch, "E16.4.2.1", {"start": v(981.07, 25.4) * mm, "end": v(949.32, 25.4) * mm});
            skLineSegment(sketch, "E16.4.2.2", {"start": v(939.8, 66.68) * mm, "end": v(939.8, 34.93) * mm});
            skArc(sketch, "E16.4.2.3", {"start": v(949.32, 76.2) * mm, "mid": v(942.59, 73.41) * mm, "end": v(939.8, 66.68) * mm});
            skLineSegment(sketch, "E16.4.2.4", {"start": v(990.6, 66.68) * mm, "end": v(990.6, 34.93) * mm});
            skLineSegment(sketch, "E16.4.2.5", {"start": v(981.07, 76.2) * mm, "end": v(949.32, 76.2) * mm});
            skArc(sketch, "E16.4.2.6", {"start": v(990.6, 66.68) * mm, "mid": v(987.81, 73.41) * mm, "end": v(981.07, 76.2) * mm});
            skArc(sketch, "E16.4.2.7", {"start": v(939.8, 34.93) * mm, "mid": v(942.59, 28.19) * mm, "end": v(949.32, 25.4) * mm});
            skArc(sketch, "E16.5.0.0", {"start": v(1184.27, 431.8) * mm, "mid": v(1191.01, 434.59) * mm, "end": v(1193.8, 441.33) * mm});
            skLineSegment(sketch, "E16.5.0.1", {"start": v(1184.27, 431.8) * mm, "end": v(1152.53, 431.8) * mm});
            skLineSegment(sketch, "E16.5.0.2", {"start": v(1143, 473.08) * mm, "end": v(1143, 441.33) * mm});
            skArc(sketch, "E16.5.0.3", {"start": v(1152.53, 482.6) * mm, "mid": v(1145.79, 479.81) * mm, "end": v(1143, 473.08) * mm});
            skLineSegment(sketch, "E16.5.0.4", {"start": v(1193.8, 473.08) * mm, "end": v(1193.8, 441.33) * mm});
            skLineSegment(sketch, "E16.5.0.5", {"start": v(1184.27, 482.6) * mm, "end": v(1152.53, 482.6) * mm});
            skArc(sketch, "E16.5.0.6", {"start": v(1193.8, 473.08) * mm, "mid": v(1191.01, 479.81) * mm, "end": v(1184.27, 482.6) * mm});
            skArc(sketch, "E16.5.0.7", {"start": v(1143, 441.33) * mm, "mid": v(1145.79, 434.59) * mm, "end": v(1152.53, 431.8) * mm});
            skArc(sketch, "E16.5.1.0", {"start": v(1184.27, 228.6) * mm, "mid": v(1191.01, 231.39) * mm, "end": v(1193.8, 238.13) * mm});
            skLineSegment(sketch, "E16.5.1.1", {"start": v(1184.27, 228.6) * mm, "end": v(1152.53, 228.6) * mm});
            skLineSegment(sketch, "E16.5.1.2", {"start": v(1143, 269.88) * mm, "end": v(1143, 238.13) * mm});
            skArc(sketch, "E16.5.1.3", {"start": v(1152.53, 279.4) * mm, "mid": v(1145.79, 276.61) * mm, "end": v(1143, 269.88) * mm});
            skLineSegment(sketch, "E16.5.1.4", {"start": v(1193.8, 269.88) * mm, "end": v(1193.8, 238.13) * mm});
            skLineSegment(sketch, "E16.5.1.5", {"start": v(1184.27, 279.4) * mm, "end": v(1152.53, 279.4) * mm});
            skArc(sketch, "E16.5.1.6", {"start": v(1193.8, 269.88) * mm, "mid": v(1191.01, 276.61) * mm, "end": v(1184.27, 279.4) * mm});
            skArc(sketch, "E16.5.1.7", {"start": v(1143, 238.13) * mm, "mid": v(1145.79, 231.39) * mm, "end": v(1152.53, 228.6) * mm});
            skArc(sketch, "E16.5.2.0", {"start": v(1184.27, 25.4) * mm, "mid": v(1191.01, 28.19) * mm, "end": v(1193.8, 34.93) * mm});
            skLineSegment(sketch, "E16.5.2.1", {"start": v(1184.27, 25.4) * mm, "end": v(1152.53, 25.4) * mm});
            skLineSegment(sketch, "E16.5.2.2", {"start": v(1143, 66.68) * mm, "end": v(1143, 34.93) * mm});
            skArc(sketch, "E16.5.2.3", {"start": v(1152.53, 76.2) * mm, "mid": v(1145.79, 73.41) * mm, "end": v(1143, 66.68) * mm});
            skLineSegment(sketch, "E16.5.2.4", {"start": v(1193.8, 66.68) * mm, "end": v(1193.8, 34.93) * mm});
            skLineSegment(sketch, "E16.5.2.5", {"start": v(1184.27, 76.2) * mm, "end": v(1152.53, 76.2) * mm});
            skArc(sketch, "E16.5.2.6", {"start": v(1193.8, 66.68) * mm, "mid": v(1191.01, 73.41) * mm, "end": v(1184.27, 76.2) * mm});
            skArc(sketch, "E16.5.2.7", {"start": v(1143, 34.93) * mm, "mid": v(1145.79, 28.19) * mm, "end": v(1152.53, 25.4) * mm});
            skLineSegment(sketch, "E16.direction1", {"start": v(127, 441.33) * mm, "end": v(330.2, 441.33) * mm, "construction": true});
            skLineSegment(sketch, "E16.direction2", {"start": v(127, 441.33) * mm, "end": v(127, 238.13) * mm, "construction": true});
            skSolve(sketch);
        }
        {
            var Q0;
            Q0 = qSketchRegion(id + "F2", true);
            extrude(context, id + "F3", {"entities" : qUnion([Q0]), "operationType" : NewBodyOperationType.ADD, "depth" : 6.35 * mm, "offsetDistance" : 25.4 * mm, "hasDraft" : true, "draftAngle" : 3 * degree});
        }
    });
